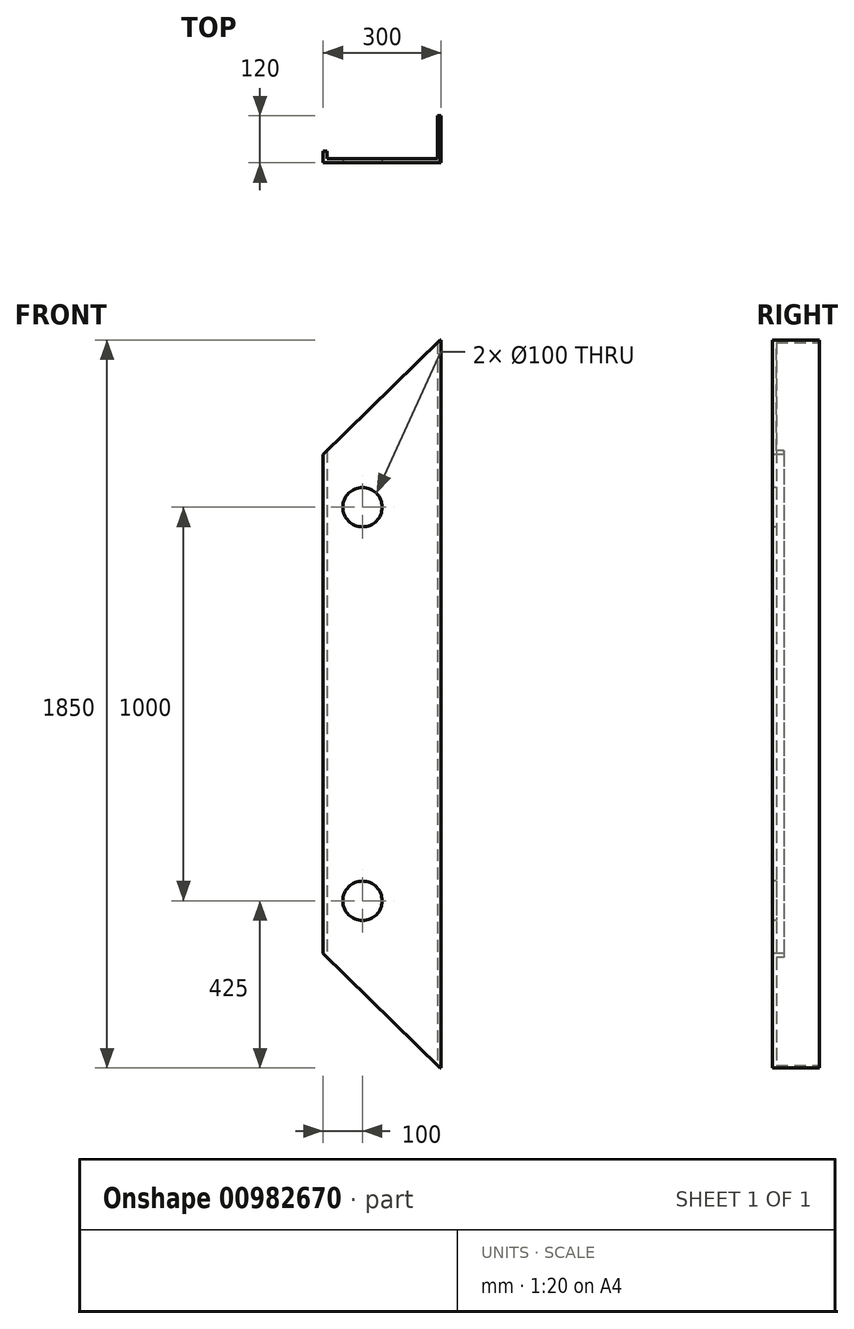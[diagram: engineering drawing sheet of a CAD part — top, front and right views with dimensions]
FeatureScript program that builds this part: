
annotation { "Feature Type Name" : "Feature", "Feature Type Description" : "" }
export const myFeature = defineFeature(function(context is Context, id is Id, definition is map)
    precondition{}
    {
        {
            var Q0;
            Q0=qCreatedBy(makeId("Top.planeOp"),FACE);
            var sketch = newSketch(context, id + "F0", { "sketchPlane" : qUnion([Q0])});
            skLineSegment(sketch, "E0", {"start": v(-110, 0) * mm, "end": v(-100, 0) * mm});
            skLineSegment(sketch, "E1", {"start": v(-100, 0) * mm, "end": v(-100, -20) * mm});
            skLineSegment(sketch, "E2", {"start": v(-100, -20) * mm, "end": v(180, -20) * mm});
            skLineSegment(sketch, "E3", {"start": v(180, -20) * mm, "end": v(180, 90) * mm});
            skLineSegment(sketch, "E4", {"start": v(180, 90) * mm, "end": v(190, 90) * mm});
            skLineSegment(sketch, "E5", {"start": v(190, 90) * mm, "end": v(190, -30) * mm});
            skLineSegment(sketch, "E6", {"start": v(190, -30) * mm, "end": v(-110, -30) * mm});
            skLineSegment(sketch, "E7", {"start": v(-110, -30) * mm, "end": v(-110, 0) * mm});
            skSolve(sketch);
        }
        {
            var Q0;
            Q0=qSketchRegion(id+"F0",true);
            extrude(context, id + "F1", {"entities" : qUnion([Q0]), "depth" : 1850 * mm, "offsetDistance" : 25 * mm});
        }
        {
            var Q0;
            Q0=makeQuery(id+"F1.opExtrude","SWEPT_FACE",FACE,{"disambiguationData":[OSD([sQuery(id+"F0.wireOp",EDGE,"E6")])]});
            var sketch = newSketch(context, id + "F2", { "sketchPlane" : qUnion([Q0])});
            skLineSegment(sketch, "E8", {"start": v(-310, 1362.11) * mm, "end": v(-310, 2050) * mm});
            skLineSegment(sketch, "E9", {"start": v(-310, 2050) * mm, "end": v(390, 2050) * mm});
            skLineSegment(sketch, "E10", {"start": v(390, 2050) * mm, "end": v(-310, 1362.11) * mm});
            skLineSegment(sketch, "E11", {"start": v(-2423.37, 925) * mm, "end": v(3096.96, 925) * mm});
            skLineSegment(sketch, "E12.MirrorCS", {"start": v(-310, -200) * mm, "end": v(390, -200) * mm});
            skLineSegment(sketch, "E13.MirrorCS", {"start": v(-310, 487.89) * mm, "end": v(-310, -200) * mm});
            skLineSegment(sketch, "E14.MirrorCS", {"start": v(390, -200) * mm, "end": v(-310, 487.89) * mm});
            skSolve(sketch);
        }
        {
            var Q0;
            {var subQ0=sQuery(id+"F2.wireOp",EDGE,"E14.MirrorCS");var subQ1=sQuery(id+"F0.wireOp",EDGE,"E6");var subQ2=makeQuery(id+"F1.opExtrude","CAP_EDGE",EDGE,{"disambiguationData":[OSD([subQ1])],"isStart":true});var subQ3=makeQuery(id+"F2.imprint","INTERSECT",VERTEX,{"derivedFrom":[subQ2,subQ0]});Q0=makeQuery(id+"F2.imprint","IMPRINT",FACE,{"disambiguationData":[TD([[makeQuery(id+"F2.imprint","IMPRINT",EDGE,{"disambiguationData":[TD([[subQ3,-1.0]])],"derivedFrom":subQ0}),1.0]])]});}
            var Q1;
            {var subQ0=sQuery(id+"F2.wireOp",EDGE,"E10");var subQ1=sQuery(id+"F0.wireOp",EDGE,"E6");var subQ2=makeQuery(id+"F1.opExtrude","CAP_EDGE",EDGE,{"disambiguationData":[OSD([subQ1])],"isStart":false});var subQ3=makeQuery(id+"F2.imprint","INTERSECT",VERTEX,{"derivedFrom":[subQ2,subQ0]});Q1=makeQuery(id+"F2.imprint","IMPRINT",FACE,{"disambiguationData":[TD([[makeQuery(id+"F2.imprint","IMPRINT",EDGE,{"disambiguationData":[TD([[subQ3,-1.0]])],"derivedFrom":subQ0}),-1.0]])]});}
            extrude(context, id + "F3", {"entities" : qUnion([Q0, Q1]), "operationType" : NewBodyOperationType.REMOVE, "oppositeDirection" : true, "depth" : 200 * mm, "offsetDistance" : 25 * mm});
        }
        {
            var Q0;
            Q0=makeQuery(id+"F1.opExtrude","SWEPT_FACE",FACE,{"disambiguationData":[OSD([sQuery(id+"F0.wireOp",EDGE,"E6")])]});
            var sketch = newSketch(context, id + "F4", { "sketchPlane" : qUnion([Q0])});
            skCircle(sketch, "E15", {"center": v(-10, 1425) * mm, "radius": 50 * mm});
            skCircle(sketch, "E16.0.1.0", {"center": v(-10, 425) * mm, "radius": 50 * mm});
            skLineSegment(sketch, "E16.direction1", {"start": v(15, 1580) * mm, "end": v(894.74, 1580) * mm, "construction": true});
            skLineSegment(sketch, "E16.direction2", {"start": v(894.74, 1580) * mm, "end": v(894.74, 780) * mm, "construction": true});
            skSolve(sketch);
        }
        {
            var Q0;
            Q0=makeQuery(id+"F4.imprint","IMPRINT",FACE,{"disambiguationData":[TD([[makeQuery(id+"F4.imprint","IMPRINT",EDGE,{"derivedFrom":sQuery(id+"F4.wireOp",EDGE,"b3d97927-093a-4395-b5cc-9a3411af9ab3.0.0.3")}),1.0]])]});
            var Q1;
            Q1=makeQuery(id+"F4.imprint","IMPRINT",FACE,{"disambiguationData":[TD([[makeQuery(id+"F4.imprint","IMPRINT",EDGE,{"derivedFrom":sQuery(id+"F4.wireOp",EDGE,"E16.0.2.0")}),1.0]])]});
            var Q2;
            Q2=makeQuery(id+"F4.imprint","IMPRINT",FACE,{"disambiguationData":[TD([[makeQuery(id+"F4.imprint","IMPRINT",EDGE,{"derivedFrom":sQuery(id+"F4.wireOp",EDGE,"E16.0.1.0")}),1.0]])]});
            var Q3;
            Q3=makeQuery(id+"F4.imprint","IMPRINT",FACE,{"disambiguationData":[TD([[makeQuery(id+"F4.imprint","IMPRINT",EDGE,{"derivedFrom":sQuery(id+"F4.wireOp",EDGE,"E15")}),1.0]])]});
            extrude(context, id + "F5", {"entities" : qUnion([Q0, Q1, Q2, Q3]), "operationType" : NewBodyOperationType.REMOVE, "endBound" : BoundingType.THROUGH_ALL, "oppositeDirection" : true, "depth" : 25 * mm, "offsetDistance" : 25 * mm});
        }
    });
